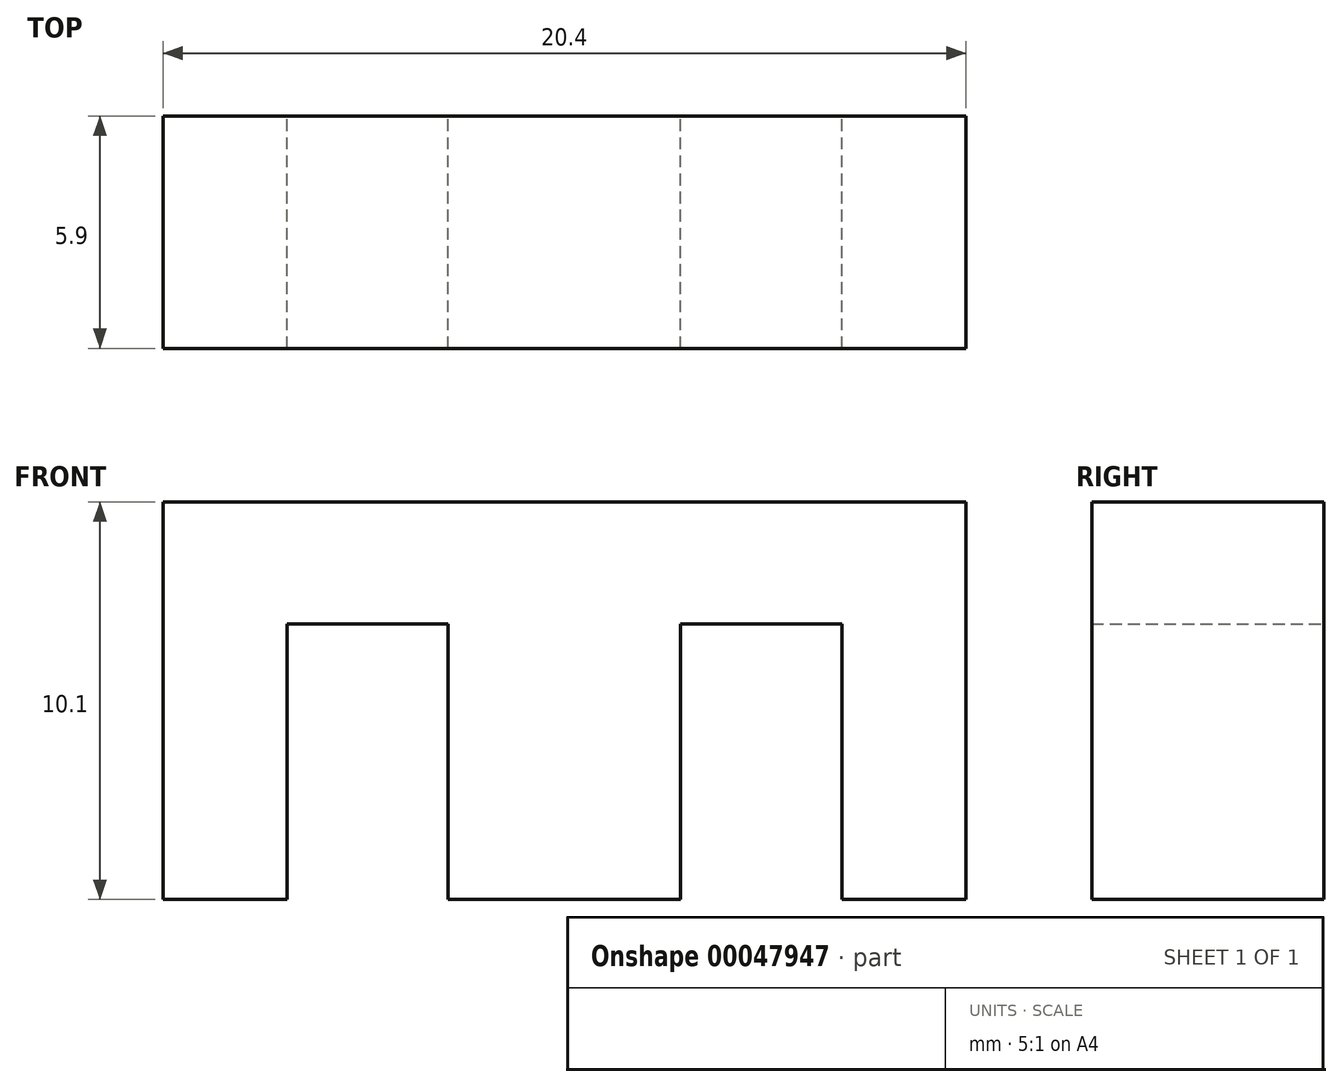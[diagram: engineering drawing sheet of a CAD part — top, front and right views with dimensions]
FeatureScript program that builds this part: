
annotation { "Feature Type Name" : "Feature", "Feature Type Description" : "" }
export const myFeature = defineFeature(function(context is Context, id is Id, definition is map)
    precondition{}
    {
        {
            var Q0;
            Q0=qCreatedBy(makeId("Front.planeOp"),FACE);
            var sketch = newSketch(context, id + "F0", { "sketchPlane" : qUnion([Q0])});
            skLineSegment(sketch, "E0", {"start": v(-10.2, 0) * mm, "end": v(-10.2, 10.1) * mm});
            skLineSegment(sketch, "E1", {"start": v(-10.2, 10.1) * mm, "end": v(10.2, 10.1) * mm});
            skLineSegment(sketch, "E2", {"start": v(10.2, 10.1) * mm, "end": v(10.2, 0) * mm});
            skLineSegment(sketch, "E3", {"start": v(10.2, 0) * mm, "end": v(7.05, 0) * mm});
            skLineSegment(sketch, "E4", {"start": v(7.05, 0) * mm, "end": v(7.05, 7) * mm});
            skLineSegment(sketch, "E5", {"start": v(7.05, 7) * mm, "end": v(2.95, 7) * mm});
            skLineSegment(sketch, "E6", {"start": v(2.95, 7) * mm, "end": v(2.95, 0) * mm});
            skLineSegment(sketch, "E7", {"start": v(2.95, 0) * mm, "end": v(-2.95, 0) * mm});
            skLineSegment(sketch, "E8", {"start": v(-2.95, 0) * mm, "end": v(-2.95, 7) * mm});
            skLineSegment(sketch, "E9", {"start": v(-2.95, 7) * mm, "end": v(-7.05, 7) * mm});
            skLineSegment(sketch, "E10", {"start": v(-7.05, 7) * mm, "end": v(-7.05, 0) * mm});
            skLineSegment(sketch, "E11", {"start": v(-7.05, 0) * mm, "end": v(-10.2, 0) * mm});
            skSolve(sketch);
        }
        {
            var Q0;
            Q0=qSketchRegion(id+"F0",true);
            extrude(context, id + "F1", {"entities" : qUnion([Q0]), "endBound" : BoundingType.SYMMETRIC, "depth" : 5.9 * mm});
        }
    });
